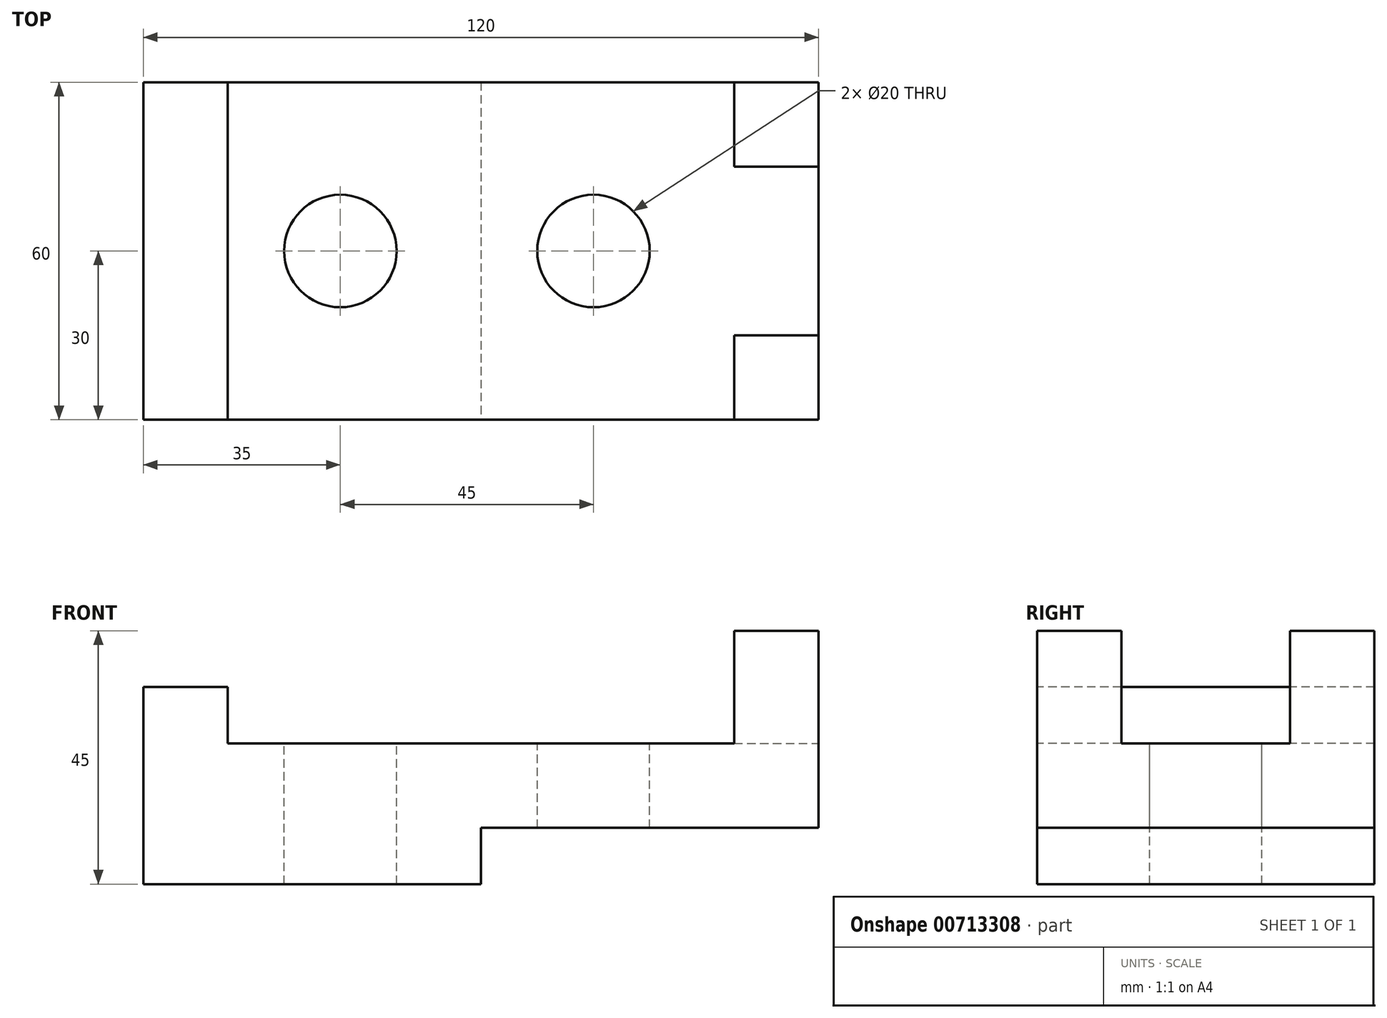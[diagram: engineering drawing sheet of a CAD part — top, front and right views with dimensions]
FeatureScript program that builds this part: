
annotation { "Feature Type Name" : "Feature", "Feature Type Description" : "" }
export const myFeature = defineFeature(function(context is Context, id is Id, definition is map)
    precondition{}
    {
        {
            var Q0;
            Q0=qCreatedBy(makeId("Front.planeOp"),FACE);
            var sketch = newSketch(context, id + "F0", { "sketchPlane" : qUnion([Q0])});
            skLineSegment(sketch, "E0", {"start": v(0, 0) * mm, "end": v(0, 35) * mm});
            skLineSegment(sketch, "E1", {"start": v(0, 35) * mm, "end": v(15, 35) * mm});
            skLineSegment(sketch, "E2", {"start": v(15, 35) * mm, "end": v(15, 25) * mm});
            skLineSegment(sketch, "E3", {"start": v(0, 0) * mm, "end": v(60, 0) * mm});
            skLineSegment(sketch, "E4", {"start": v(60, 0) * mm, "end": v(60, 10) * mm});
            skLineSegment(sketch, "E5", {"start": v(60, 10) * mm, "end": v(120, 10) * mm});
            skLineSegment(sketch, "E6", {"start": v(120, 10) * mm, "end": v(120, 45) * mm});
            skPoint(sketch, "E7.end.orphan", {"position": v(15, 15) * mm});
            skPoint(sketch, "E8.orphan", {"position": v(105, 25) * mm});
            skPoint(sketch, "E9.end.orphan", {"position": v(105, 35) * mm});
            skPoint(sketch, "E10.end.orphan", {"position": v(105, 45) * mm});
            skLineSegment(sketch, "E11", {"start": v(120, 45) * mm, "end": v(105, 45) * mm});
            skLineSegment(sketch, "E12", {"start": v(105, 45) * mm, "end": v(105, 25) * mm});
            skLineSegment(sketch, "E13", {"start": v(15, 25) * mm, "end": v(105, 25) * mm});
            skSolve(sketch);
        }
        {
            var Q0;
            Q0 = qSketchRegion(id + "F0", true);
            extrude(context, id + "F1", {"entities" : qUnion([Q0]), "oppositeDirection" : true, "depth" : 60 * mm, "offsetDistance" : 25 * mm});
        }
        {
            var Q0;
            Q0=makeQuery(id+"F1.opExtrude","SWEPT_FACE",FACE,{"disambiguationData":[OSD([sQuery(id+"F0.wireOp",EDGE,"E6")])]});
            var sketch = newSketch(context, id + "F2", { "sketchPlane" : qUnion([Q0])});
            skLineSegment(sketch, "E14", {"start": v(0, 45) * mm, "end": v(15, 45) * mm});
            skLineSegment(sketch, "E15", {"start": v(15, 45) * mm, "end": v(15, 25) * mm});
            skLineSegment(sketch, "E16", {"start": v(15, 25) * mm, "end": v(45, 25) * mm});
            skLineSegment(sketch, "E17", {"start": v(45, 25) * mm, "end": v(45, 45) * mm});
            skLineSegment(sketch, "E18.0.0", {"start": v(0, 45) * mm, "end": v(0, 10) * mm});
            skLineSegment(sketch, "E18.0.1", {"start": v(0, 10) * mm, "end": v(60, 10) * mm});
            skLineSegment(sketch, "E18.0.2", {"start": v(60, 10) * mm, "end": v(60, 45) * mm});
            skLineSegment(sketch, "E18.0.3", {"start": v(60, 45) * mm, "end": v(0, 45) * mm});
            skLineSegment(sketch, "E19", {"start": v(45, 45) * mm, "end": v(15, 45) * mm});
            skSolve(sketch);
        }
        {
            var Q0;
            Q0=makeQuery(id+"F2.imprint","IMPRINT",FACE,{"disambiguationData":[TD([[makeQuery(id+"F2.imprint","IMPRINT",EDGE,{"derivedFrom":sQuery(id+"F2.wireOp",EDGE,"E15")}),1.0]])]});
            extrude(context, id + "F3", {"entities" : qUnion([Q0]), "operationType" : NewBodyOperationType.REMOVE, "oppositeDirection" : true, "depth" : 25 * mm, "offsetDistance" : 25 * mm});
        }
        {
            var Q0;
            Q0=makeQuery(id+"F3.boolean.opBoolean","MERGE",FACE,{"derivedFrom":[makeQuery(id+"F1.opExtrude","SWEPT_FACE",FACE,{"disambiguationData":[OSD([sQuery(id+"F0.wireOp",EDGE,"E13")])]}),makeQuery(id+"F3.opExtrude","SWEPT_FACE",FACE,{"disambiguationData":[OSD([sQuery(id+"F2.wireOp",EDGE,"E16")])]})]});
            var sketch = newSketch(context, id + "F4", { "sketchPlane" : qUnion([Q0])});
            skCircle(sketch, "E20", {"center": v(35, 30) * mm, "radius": 10 * mm});
            skCircle(sketch, "E21", {"center": v(80, 30) * mm, "radius": 10 * mm});
            skSolve(sketch);
        }
        {
            var Q0;
            Q0 = qSketchRegion(id + "F4", true);
            extrude(context, id + "F5", {"entities" : qUnion([Q0]), "operationType" : NewBodyOperationType.REMOVE, "endBound" : BoundingType.THROUGH_ALL, "oppositeDirection" : true, "depth" : 25 * mm, "offsetDistance" : 25 * mm});
        }
    });
